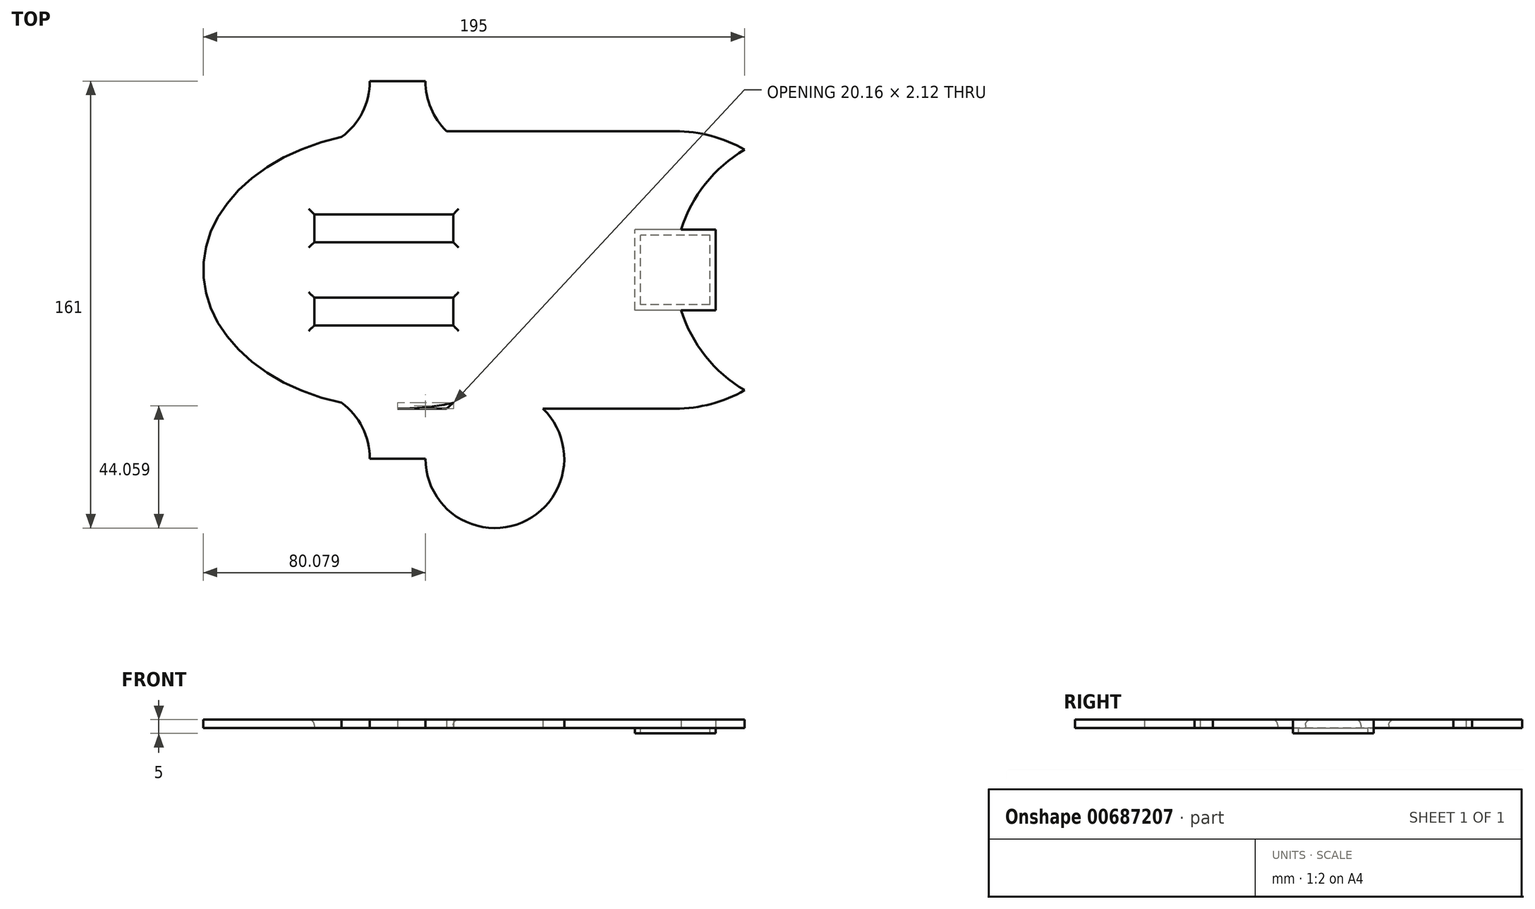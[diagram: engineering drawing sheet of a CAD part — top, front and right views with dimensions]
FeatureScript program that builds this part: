
annotation { "Feature Type Name" : "Feature", "Feature Type Description" : "" }
export const myFeature = defineFeature(function(context is Context, id is Id, definition is map)
    precondition{}
    {
        {
            var Q0;
            Q0=qCreatedBy(makeId("Top.planeOp"),FACE);
            var sketch = newSketch(context, id + "F0", { "sketchPlane" : qUnion([Q0])});
            skLineSegment(sketch, "E0.bottom", {"start": v(0, 0) * mm, "end": v(100, 0) * mm});
            skLineSegment(sketch, "E0.top", {"start": v(0, 100) * mm, "end": v(100, 100) * mm});
            skLineSegment(sketch, "E0.left", {"start": v(0, 0) * mm, "end": v(0, 30) * mm});
            skLineSegment(sketch, "E1", {"start": v(0, 50) * mm, "end": v(-70, 50) * mm});
            skEllipse(sketch, "E2", {"center": v(0, 50) * mm, "majorRadius": 50 * mm, "minorRadius": 70 * mm, "majorAxis": v(0, 1)});
            skLineSegment(sketch, "E3", {"start": v(0, 100) * mm, "end": v(0, 118) * mm});
            skLineSegment(sketch, "E4", {"start": v(0, 118) * mm, "end": v(10, 118) * mm});
            skLineSegment(sketch, "E5", {"start": v(0, 118) * mm, "end": v(-10, 118) * mm});
            skLineSegment(sketch, "E6", {"start": v(-10, 118) * mm, "end": v(-35, 118) * mm});
            skLineSegment(sketch, "E7", {"start": v(10, 118) * mm, "end": v(35, 118) * mm});
            skArc(sketch, "E8", {"start": v(-20.16, 97.88) * mm, "mid": v(-12.68, 106.73) * mm, "end": v(-10, 118) * mm});
            skCircle(sketch, "E9", {"center": v(35, 118) * mm, "radius": 25 * mm});
            skArc(sketch, "E10.MirrorC", {"start": v(-35.7, 93) * mm, "mid": v(-42.48, 141.85) * mm, "end": v(-20.16, 97.88) * mm});
            skCircle(sketch, "E11.MirrorC", {"center": v(-35, -18) * mm, "radius": 25 * mm});
            skLineSegment(sketch, "E12.MirrorCS", {"start": v(-10, -18) * mm, "end": v(-35, -18) * mm});
            skLineSegment(sketch, "E13.MirrorCS", {"start": v(0, -18) * mm, "end": v(10, -18) * mm});
            skLineSegment(sketch, "E14.MirrorCS", {"start": v(0, -18) * mm, "end": v(-10, -18) * mm});
            skLineSegment(sketch, "E15.MirrorCS", {"start": v(0, 0) * mm, "end": v(0, -18) * mm});
            skCircle(sketch, "E16.MirrorC", {"center": v(35, -18) * mm, "radius": 25 * mm});
            skLineSegment(sketch, "E17.MirrorCS", {"start": v(10, -18) * mm, "end": v(35, -18) * mm});
            skArc(sketch, "E18", {"start": v(-10, 118) * mm, "mid": v(-12.68, 106.73) * mm, "end": v(-20.16, 97.88) * mm});
            skLineSegment(sketch, "E19", {"start": v(150, 50) * mm, "end": v(0, 50) * mm});
            skArc(sketch, "E20", {"start": v(125, 93.3) * mm, "mid": v(100, 50) * mm, "end": v(125, 6.7) * mm});
            skCircle(sketch, "E21", {"center": v(100, 50) * mm, "radius": 50 * mm});
            skLineSegment(sketch, "E22", {"start": v(0, 50) * mm, "end": v(0, 60) * mm});
            skLineSegment(sketch, "E23", {"start": v(0, 60) * mm, "end": v(-10, 60) * mm});
            skLineSegment(sketch, "E24", {"start": v(-10, 40) * mm, "end": v(0, 40) * mm});
            skLineSegment(sketch, "E25.top", {"start": v(0, 70) * mm, "end": v(-10, 70) * mm});
            skLineSegment(sketch, "E26.top", {"start": v(-10, 30) * mm, "end": v(0, 30) * mm});
            skLineSegment(sketch, "E27", {"start": v(-10, 70) * mm, "end": v(-30, 70) * mm});
            skLineSegment(sketch, "E28", {"start": v(-30, 70) * mm, "end": v(-30, 60) * mm});
            skLineSegment(sketch, "E29", {"start": v(-30, 60) * mm, "end": v(-10, 60) * mm});
            skLineSegment(sketch, "E30", {"start": v(0, 70) * mm, "end": v(20, 70) * mm});
            skLineSegment(sketch, "E31", {"start": v(20, 70) * mm, "end": v(20, 60) * mm});
            skLineSegment(sketch, "E32", {"start": v(20, 60) * mm, "end": v(0, 60) * mm});
            skLineSegment(sketch, "E33", {"start": v(-10, 40) * mm, "end": v(-30, 40) * mm});
            skLineSegment(sketch, "E34", {"start": v(-30, 40) * mm, "end": v(-30, 30) * mm});
            skLineSegment(sketch, "E35", {"start": v(-30, 30) * mm, "end": v(20, 30) * mm});
            skLineSegment(sketch, "E36", {"start": v(20, 30) * mm, "end": v(20, 40) * mm});
            skLineSegment(sketch, "E37", {"start": v(20, 40) * mm, "end": v(0, 40) * mm});
            skLineSegment(sketch, "E38", {"start": v(0, 40) * mm, "end": v(0, 60) * mm});
            skLineSegment(sketch, "E39", {"start": v(0, 70) * mm, "end": v(0, 100) * mm});
            skPoint(sketch, "E40.orphan", {"position": v(150, 100) * mm});
            skLineSegment(sketch, "E41.bottom", {"start": v(112.5, 37.5) * mm, "end": v(87.5, 37.5) * mm});
            skLineSegment(sketch, "E41.top", {"start": v(112.5, 62.5) * mm, "end": v(87.5, 62.5) * mm});
            skLineSegment(sketch, "E41.left", {"start": v(112.5, 37.5) * mm, "end": v(112.5, 62.5) * mm});
            skLineSegment(sketch, "E41.right", {"start": v(87.5, 37.5) * mm, "end": v(87.5, 62.5) * mm});
            skLineSegment(sketch, "E42.0", {"start": v(114.5, 64.5) * mm, "end": v(85.5, 64.5) * mm});
            skLineSegment(sketch, "E42.1", {"start": v(114.5, 35.5) * mm, "end": v(114.5, 64.5) * mm});
            skLineSegment(sketch, "E42.2", {"start": v(114.5, 35.5) * mm, "end": v(85.5, 35.5) * mm});
            skLineSegment(sketch, "E42.3", {"start": v(85.5, 35.5) * mm, "end": v(85.5, 64.5) * mm});
            skSolve(sketch);
        }
        {
            var Q0;
            {var subQ0=sQuery(id+"F0.wireOp",EDGE,"E11.MirrorC");var subQ1=sQuery(id+"F0.wireOp",EDGE,"E2");var subQ2=makeQuery(id+"F0.imprint","INTERSECT",VERTEX,{"disambiguationData":[OD(0.0)],"derivedFrom":[subQ1,subQ0]});Q0=makeQuery(id+"F0.imprint","IMPRINT",FACE,{"disambiguationData":[TD([[makeQuery(id+"F0.imprint","IMPRINT",EDGE,{"disambiguationData":[TD([[subQ2,-1.0]])],"derivedFrom":subQ1}),1.0]])]});}
            var Q1;
            {var subQ4=sQuery(id+"F0.wireOp",EDGE,"E13.MirrorCS");Q1=makeQuery(id+"F0.imprint","IMPRINT",FACE,{"disambiguationData":[TD([[makeQuery(id+"F0.imprint","IMPRINT",EDGE,{"derivedFrom":subQ4}),1.0]])]});}
            var Q2;
            {var subQ0=sQuery(id+"F0.wireOp",EDGE,"E21");var subQ1=sQuery(id+"F0.wireOp",EDGE,"E0.bottom");var subQ2=makeQuery(id+"F0.imprint","INTERSECT",VERTEX,{"derivedFrom":[subQ1,subQ0]});Q2=makeQuery(id+"F0.imprint","IMPRINT",FACE,{"disambiguationData":[TD([[makeQuery(id+"F0.imprint","IMPRINT",EDGE,{"disambiguationData":[TD([[subQ2,1.0]])],"derivedFrom":subQ1}),1.0]])]});}
            var Q3;
            {var subQ0=sQuery(id+"F0.wireOp",EDGE,"E3");Q3=makeQuery(id+"F0.imprint","IMPRINT",FACE,{"disambiguationData":[TD([[makeQuery(id+"F0.imprint","IMPRINT",EDGE,{"derivedFrom":subQ0}),-1.0]])]});}
            var Q4;
            {var subQ0=sQuery(id+"F0.wireOp",EDGE,"E21");var subQ1=sQuery(id+"F0.wireOp",EDGE,"E0.top");var subQ2=makeQuery(id+"F0.imprint","INTERSECT",VERTEX,{"derivedFrom":[subQ1,subQ0]});Q4=makeQuery(id+"F0.imprint","IMPRINT",FACE,{"disambiguationData":[TD([[makeQuery(id+"F0.imprint","IMPRINT",EDGE,{"disambiguationData":[TD([[subQ2,1.0]])],"derivedFrom":subQ1}),-1.0]])]});}
            var Q5;
            {var subQ4=sQuery(id+"F0.wireOp",EDGE,"E14.MirrorCS");Q5=makeQuery(id+"F0.imprint","IMPRINT",FACE,{"disambiguationData":[TD([[makeQuery(id+"F0.imprint","IMPRINT",EDGE,{"derivedFrom":subQ4}),-1.0]])]});}
            var Q6;
            {var subQ0=sQuery(id+"F0.wireOp",EDGE,"E3");Q6=makeQuery(id+"F0.imprint","IMPRINT",FACE,{"disambiguationData":[TD([[makeQuery(id+"F0.imprint","IMPRINT",EDGE,{"derivedFrom":subQ0}),1.0]])]});}
            var Q7;
            {var subQ5=sQuery(id+"F0.wireOp",EDGE,"E21");var subQ6=sQuery(id+"F0.wireOp",EDGE,"E19");var subQ7=makeQuery(id+"F0.imprint","INTERSECT",VERTEX,{"disambiguationData":[OD(0.0)],"derivedFrom":[subQ6,subQ5]});Q7=makeQuery(id+"F0.imprint","IMPRINT",FACE,{"disambiguationData":[TD([[makeQuery(id+"F0.imprint","IMPRINT",EDGE,{"disambiguationData":[TD([[subQ7,-1.0]])],"derivedFrom":subQ6}),-1.0]])]});}
            var Q8;
            {var subQ3=sQuery(id+"F0.wireOp",EDGE,"E19");var subQ5=sQuery(id+"F0.wireOp",EDGE,"E21");var subQ6=makeQuery(id+"F0.imprint","INTERSECT",VERTEX,{"disambiguationData":[OD(0.0)],"derivedFrom":[subQ3,subQ5]});Q8=makeQuery(id+"F0.imprint","IMPRINT",FACE,{"disambiguationData":[TD([[makeQuery(id+"F0.imprint","IMPRINT",EDGE,{"disambiguationData":[TD([[subQ6,-1.0]])],"derivedFrom":subQ3}),1.0]])]});}
            var Q9;
            {var subQ0=sQuery(id+"F0.wireOp",EDGE,"E16.MirrorC");var subQ1=sQuery(id+"F0.wireOp",EDGE,"E0.bottom");var subQ2=makeQuery(id+"F0.imprint","INTERSECT",VERTEX,{"disambiguationData":[OD(0.0)],"derivedFrom":[subQ1,subQ0]});Q9=makeQuery(id+"F0.imprint","IMPRINT",FACE,{"disambiguationData":[TD([[makeQuery(id+"F0.imprint","IMPRINT",EDGE,{"disambiguationData":[TD([[subQ2,1.0]])],"derivedFrom":subQ1}),1.0]])]});}
            var Q10;
            {var subQ0=sQuery(id+"F0.wireOp",EDGE,"E9");var subQ1=sQuery(id+"F0.wireOp",EDGE,"E0.top");var subQ2=makeQuery(id+"F0.imprint","INTERSECT",VERTEX,{"disambiguationData":[OD(0.0)],"derivedFrom":[subQ1,subQ0]});Q10=makeQuery(id+"F0.imprint","IMPRINT",FACE,{"disambiguationData":[TD([[makeQuery(id+"F0.imprint","IMPRINT",EDGE,{"disambiguationData":[TD([[subQ2,1.0]])],"derivedFrom":subQ1}),-1.0]])]});}
            var Q11;
            {var subQ1=sQuery(id+"F0.wireOp",EDGE,"E0.left");Q11=makeQuery(id+"F0.imprint","IMPRINT",FACE,{"disambiguationData":[TD([[makeQuery(id+"F0.imprint","IMPRINT",EDGE,{"derivedFrom":subQ1}),1.0]])]});}
            var Q12;
            {var subQ1=sQuery(id+"F0.wireOp",EDGE,"E1");Q12=makeQuery(id+"F0.imprint","IMPRINT",FACE,{"disambiguationData":[TD([[makeQuery(id+"F0.imprint","IMPRINT",EDGE,{"derivedFrom":subQ1}),-1.0]])]});}
            var Q13;
            {var subQ0=sQuery(id+"F0.wireOp",EDGE,"E21");var subQ2=sQuery(id+"F0.wireOp",EDGE,"E2");var subQ3=makeQuery(id+"F0.imprint","INTERSECT",VERTEX,{"disambiguationData":[OD(0.0)],"derivedFrom":[subQ2,subQ0]});Q13=makeQuery(id+"F0.imprint","IMPRINT",FACE,{"disambiguationData":[TD([[makeQuery(id+"F0.imprint","IMPRINT",EDGE,{"disambiguationData":[TD([[subQ3,-1.0]])],"derivedFrom":subQ2}),-1.0]])]});}
            var Q14;
            {var subQ6=sQuery(id+"F0.wireOp",EDGE,"E19");var subQ7=sQuery(id+"F0.wireOp",EDGE,"E2");var subQ8=makeQuery(id+"F0.imprint","INTERSECT",VERTEX,{"derivedFrom":[subQ7,subQ6]});Q14=makeQuery(id+"F0.imprint","IMPRINT",FACE,{"disambiguationData":[TD([[makeQuery(id+"F0.imprint","IMPRINT",EDGE,{"disambiguationData":[TD([[subQ8,-1.0]])],"derivedFrom":subQ7}),-1.0]])]});}
            var Q15;
            Q15=makeQuery(id+"F0.imprint","IMPRINT",FACE,{"disambiguationData":[TD([[makeQuery(id+"F0.imprint","IMPRINT",EDGE,{"derivedFrom":sQuery(id+"F0.wireOp",EDGE,"E30")}),1.0]])]});
            var Q16;
            {var subQ0=sQuery(id+"F0.wireOp",EDGE,"E19");var subQ1=sQuery(id+"F0.wireOp",EDGE,"E2");var subQ2=makeQuery(id+"F0.imprint","INTERSECT",VERTEX,{"derivedFrom":[subQ1,subQ0]});Q16=makeQuery(id+"F0.imprint","IMPRINT",FACE,{"disambiguationData":[TD([[makeQuery(id+"F0.imprint","IMPRINT",EDGE,{"disambiguationData":[TD([[subQ2,-1.0]])],"derivedFrom":subQ1}),1.0]])]});}
            var Q17;
            {var subQ0=sQuery(id+"F0.wireOp",EDGE,"E21");var subQ1=sQuery(id+"F0.wireOp",EDGE,"E2");var subQ2=makeQuery(id+"F0.imprint","INTERSECT",VERTEX,{"disambiguationData":[OD(0.0)],"derivedFrom":[subQ1,subQ0]});Q17=makeQuery(id+"F0.imprint","IMPRINT",FACE,{"disambiguationData":[TD([[makeQuery(id+"F0.imprint","IMPRINT",EDGE,{"disambiguationData":[TD([[subQ2,-1.0]])],"derivedFrom":subQ1}),1.0]])]});}
            var Q18;
            {var subQ4=sQuery(id+"F0.wireOp",EDGE,"E0.left");Q18=makeQuery(id+"F0.imprint","IMPRINT",FACE,{"disambiguationData":[TD([[makeQuery(id+"F0.imprint","IMPRINT",EDGE,{"derivedFrom":subQ4}),-1.0]])]});}
            var Q19;
            {var subQ1=sQuery(id+"F0.wireOp",EDGE,"E0.top");var subQ3=sQuery(id+"F0.wireOp",EDGE,"E9");var subQ4=makeQuery(id+"F0.imprint","INTERSECT",VERTEX,{"disambiguationData":[OD(1.0)],"derivedFrom":[subQ1,subQ3]});Q19=makeQuery(id+"F0.imprint","IMPRINT",FACE,{"disambiguationData":[TD([[makeQuery(id+"F0.imprint","IMPRINT",EDGE,{"disambiguationData":[TD([[subQ4,-1.0]])],"derivedFrom":subQ3}),-1.0]])]});}
            var Q20;
            {var subQ0=sQuery(id+"F0.wireOp",EDGE,"E9");var subQ1=sQuery(id+"F0.wireOp",EDGE,"E2");var subQ2=makeQuery(id+"F0.imprint","INTERSECT",VERTEX,{"disambiguationData":[OD(0.0)],"derivedFrom":[subQ1,subQ0]});Q20=makeQuery(id+"F0.imprint","IMPRINT",FACE,{"disambiguationData":[TD([[makeQuery(id+"F0.imprint","IMPRINT",EDGE,{"disambiguationData":[TD([[subQ2,-1.0]])],"derivedFrom":subQ1}),1.0]])]});}
            var Q21;
            {var subQ1=sQuery(id+"F0.wireOp",EDGE,"E0.bottom");var subQ3=sQuery(id+"F0.wireOp",EDGE,"E16.MirrorC");var subQ4=makeQuery(id+"F0.imprint","INTERSECT",VERTEX,{"disambiguationData":[OD(1.0)],"derivedFrom":[subQ1,subQ3]});Q21=makeQuery(id+"F0.imprint","IMPRINT",FACE,{"disambiguationData":[TD([[makeQuery(id+"F0.imprint","IMPRINT",EDGE,{"disambiguationData":[TD([[subQ4,-1.0]])],"derivedFrom":subQ3}),1.0]])]});}
            var Q22;
            {var subQ0=sQuery(id+"F0.wireOp",EDGE,"E16.MirrorC");var subQ1=sQuery(id+"F0.wireOp",EDGE,"E2");var subQ2=makeQuery(id+"F0.imprint","INTERSECT",VERTEX,{"disambiguationData":[OD(0.0)],"derivedFrom":[subQ1,subQ0]});Q22=makeQuery(id+"F0.imprint","IMPRINT",FACE,{"disambiguationData":[TD([[makeQuery(id+"F0.imprint","IMPRINT",EDGE,{"disambiguationData":[TD([[subQ2,-1.0]])],"derivedFrom":subQ1}),1.0]])]});}
            var Q23;
            {var subQ3=sQuery(id+"F0.wireOp",EDGE,"E19");var subQ9=sQuery(id+"F0.wireOp",EDGE,"E42.1");var subQ10=makeQuery(id+"F0.imprint","INTERSECT",VERTEX,{"derivedFrom":[subQ3,subQ9]});Q23=makeQuery(id+"F0.imprint","IMPRINT",FACE,{"disambiguationData":[TD([[makeQuery(id+"F0.imprint","IMPRINT",EDGE,{"disambiguationData":[TD([[subQ10,-1.0]])],"derivedFrom":subQ3}),1.0]])]});}
            var Q24;
            {var subQ0=sQuery(id+"F0.wireOp",EDGE,"E41.right");var subQ3=sQuery(id+"F0.wireOp",EDGE,"E19");var subQ4=makeQuery(id+"F0.imprint","INTERSECT",VERTEX,{"derivedFrom":[subQ3,subQ0]});Q24=makeQuery(id+"F0.imprint","IMPRINT",FACE,{"disambiguationData":[TD([[makeQuery(id+"F0.imprint","IMPRINT",EDGE,{"disambiguationData":[TD([[subQ4,-1.0]])],"derivedFrom":subQ3}),1.0]])]});}
            var Q25;
            {var subQ0=sQuery(id+"F0.wireOp",EDGE,"E20");var subQ1=sQuery(id+"F0.wireOp",EDGE,"E19");var subQ2=makeQuery(id+"F0.imprint","INTERSECT",VERTEX,{"derivedFrom":[subQ1,subQ0]});Q25=makeQuery(id+"F0.imprint","IMPRINT",FACE,{"disambiguationData":[TD([[makeQuery(id+"F0.imprint","IMPRINT",EDGE,{"disambiguationData":[TD([[subQ2,-1.0]])],"derivedFrom":subQ1}),1.0]])]});}
            var Q26;
            {var subQ0=sQuery(id+"F0.wireOp",EDGE,"E20");var subQ1=sQuery(id+"F0.wireOp",EDGE,"E19");var subQ2=makeQuery(id+"F0.imprint","INTERSECT",VERTEX,{"derivedFrom":[subQ1,subQ0]});Q26=makeQuery(id+"F0.imprint","IMPRINT",FACE,{"disambiguationData":[TD([[makeQuery(id+"F0.imprint","IMPRINT",EDGE,{"disambiguationData":[TD([[subQ2,-1.0]])],"derivedFrom":subQ1}),-1.0]])]});}
            var Q27;
            {var subQ7=sQuery(id+"F0.wireOp",EDGE,"E19");var subQ9=sQuery(id+"F0.wireOp",EDGE,"E42.1");var subQ10=makeQuery(id+"F0.imprint","INTERSECT",VERTEX,{"derivedFrom":[subQ7,subQ9]});Q27=makeQuery(id+"F0.imprint","IMPRINT",FACE,{"disambiguationData":[TD([[makeQuery(id+"F0.imprint","IMPRINT",EDGE,{"disambiguationData":[TD([[subQ10,-1.0]])],"derivedFrom":subQ7}),-1.0]])]});}
            var Q28;
            {var subQ0=sQuery(id+"F0.wireOp",EDGE,"E41.left");var subQ1=sQuery(id+"F0.wireOp",EDGE,"E19");var subQ2=makeQuery(id+"F0.imprint","INTERSECT",VERTEX,{"derivedFrom":[subQ1,subQ0]});Q28=makeQuery(id+"F0.imprint","IMPRINT",FACE,{"disambiguationData":[TD([[makeQuery(id+"F0.imprint","IMPRINT",EDGE,{"disambiguationData":[TD([[subQ2,-1.0]])],"derivedFrom":subQ1}),1.0]])]});}
            var Q29;
            {var subQ0=sQuery(id+"F0.wireOp",EDGE,"E41.left");var subQ1=sQuery(id+"F0.wireOp",EDGE,"E19");var subQ2=makeQuery(id+"F0.imprint","INTERSECT",VERTEX,{"derivedFrom":[subQ1,subQ0]});Q29=makeQuery(id+"F0.imprint","IMPRINT",FACE,{"disambiguationData":[TD([[makeQuery(id+"F0.imprint","IMPRINT",EDGE,{"disambiguationData":[TD([[subQ2,-1.0]])],"derivedFrom":subQ1}),-1.0]])]});}
            var Q30;
            {var subQ0=sQuery(id+"F0.wireOp",EDGE,"E41.right");var subQ3=sQuery(id+"F0.wireOp",EDGE,"E19");var subQ4=makeQuery(id+"F0.imprint","INTERSECT",VERTEX,{"derivedFrom":[subQ3,subQ0]});Q30=makeQuery(id+"F0.imprint","IMPRINT",FACE,{"disambiguationData":[TD([[makeQuery(id+"F0.imprint","IMPRINT",EDGE,{"disambiguationData":[TD([[subQ4,-1.0]])],"derivedFrom":subQ3}),-1.0]])]});}
            extrude(context, id + "F1", {"entities" : qUnion([Q0, Q1, Q2, Q3, Q4, Q5, Q6, Q7, Q8, Q9, Q10, Q11, Q12, Q13, Q14, Q15, Q16, Q17, Q18, Q19, Q20, Q21, Q22, Q23, Q24, Q25, Q26, Q27, Q28, Q29, Q30]), "depth" : 3 * mm, "offsetDistance" : 25 * mm});
        }
        {
            var Q0;
            Q0=makeQuery(id+"F1.opExtrude","CAP_EDGE",EDGE,{"disambiguationData":[OSD([sQuery(id+"F0.wireOp",EDGE,"E31")])],"isStart":false});
            var Q1;
            Q1=makeQuery(id+"F1.opExtrude","CAP_EDGE",EDGE,{"disambiguationData":[OSD([sQuery(id+"F0.wireOp",EDGE,"E36")])],"isStart":false});
            var Q2;
            Q2=makeQuery(id+"F1.opExtrude","CAP_EDGE",EDGE,{"disambiguationData":[OSD([sQuery(id+"F0.wireOp",EDGE,"E24"),sQuery(id+"F0.wireOp",EDGE,"E33"),sQuery(id+"F0.wireOp",EDGE,"E37")])],"isStart":false});
            var Q3;
            Q3=makeQuery(id+"F1.opExtrude","CAP_EDGE",EDGE,{"disambiguationData":[OSD([sQuery(id+"F0.wireOp",EDGE,"E23"),sQuery(id+"F0.wireOp",EDGE,"E29"),sQuery(id+"F0.wireOp",EDGE,"E32")])],"isStart":false});
            var Q4;
            Q4=makeQuery(id+"F1.opExtrude","CAP_EDGE",EDGE,{"disambiguationData":[OSD([sQuery(id+"F0.wireOp",EDGE,"E35")])],"isStart":false});
            var Q5;
            Q5=makeQuery(id+"F1.opExtrude","CAP_EDGE",EDGE,{"disambiguationData":[OSD([sQuery(id+"F0.wireOp",EDGE,"E34")])],"isStart":false});
            var Q6;
            Q6=makeQuery(id+"F1.opExtrude","CAP_EDGE",EDGE,{"disambiguationData":[OSD([sQuery(id+"F0.wireOp",EDGE,"E28")])],"isStart":false});
            var Q7;
            Q7=makeQuery(id+"F1.opExtrude","CAP_EDGE",EDGE,{"disambiguationData":[OSD([sQuery(id+"F0.wireOp",EDGE,"E25.top"),sQuery(id+"F0.wireOp",EDGE,"E27"),sQuery(id+"F0.wireOp",EDGE,"E30")])],"isStart":false});
            var Q8;
            Q8=makeQuery(id+"FWjQsiPRKmnbxU6_1.boolean.opBoolean","COPY",EDGE,{"derivedFrom":makeQuery(id+"FWjQsiPRKmnbxU6_1.opExtrude","CAP_EDGE",EDGE,{"disambiguationData":[OSD([sQuery(id+"FoRDWVH2EN1YLIM_1.wireOp",EDGE,"Fo7FTBvF-OatF-Ye8v-invw-BYf8DDfDNs5p")])],"isStart":true})});
            var Q9;
            Q9=makeQuery(id+"FWjQsiPRKmnbxU6_1.boolean.opBoolean","INTERSECT",EDGE,{"derivedFrom":[makeQuery(id+"FhsavfPUiMTL5cG_1.opExtrude","SWEPT_FACE",FACE,{"disambiguationData":[OSD([sQuery(id+"FaphtbvGcqO1CS2_1.wireOp",EDGE,"SVR6mZwb-6mZz-pFOT-4R3M-2uJUIevgwBhd.right"),sQuery(id+"FaphtbvGcqO1CS2_1.wireOp",EDGE,"BLSzf8hX-9h4d-mfL5-Iacp-5Haw44lP9nYf.left")])]}),makeQuery(id+"FWjQsiPRKmnbxU6_1.opExtrude","SWEPT_FACE",FACE,{"disambiguationData":[OSD([sQuery(id+"FoRDWVH2EN1YLIM_1.wireOp",EDGE,"Fo7FTBvF-OatF-Ye8v-invw-BYf8DDfDNs5p")])]})]});
            var Q10;
            Q10=makeQuery(id+"FWjQsiPRKmnbxU6_1.boolean.opBoolean","COPY",EDGE,{"derivedFrom":makeQuery(id+"FWjQsiPRKmnbxU6_1.opExtrude","CAP_EDGE",EDGE,{"disambiguationData":[OSD([sQuery(id+"FoRDWVH2EN1YLIM_1.wireOp",EDGE,"f88abefe-f133-40e1-8b6e-ae7882c6de267.MirrorC")])],"isStart":true})});
            var Q11;
            Q11=makeQuery(id+"FWjQsiPRKmnbxU6_1.boolean.opBoolean","INTERSECT",EDGE,{"derivedFrom":[makeQuery(id+"FhsavfPUiMTL5cG_1.opExtrude","SWEPT_FACE",FACE,{"disambiguationData":[OSD([sQuery(id+"FaphtbvGcqO1CS2_1.wireOp",EDGE,"aa437bf4-4790-4772-8fad-b6166ee4a9c60.MirrorCS"),sQuery(id+"FaphtbvGcqO1CS2_1.wireOp",EDGE,"c2af337a-7aa6-4700-ac16-6fe0a1636ed80.MirrorCS")])]}),makeQuery(id+"FWjQsiPRKmnbxU6_1.opExtrude","SWEPT_FACE",FACE,{"disambiguationData":[OSD([sQuery(id+"FoRDWVH2EN1YLIM_1.wireOp",EDGE,"f88abefe-f133-40e1-8b6e-ae7882c6de267.MirrorC")])]})]});
            fillet(context, id + "F2", {"entities" : qUnion([Q0, Q1, Q2, Q3, Q4, Q5, Q6, Q7, Q8, Q9, Q10, Q11]), "radius" : 2 * mm, "tangentPropagation" : true, "allowEdgeOverflow" : false});
        }
        {
            var Q0;
            {var subQ0=sQuery(id+"F0.wireOp",EDGE,"E41.right");var subQ3=sQuery(id+"F0.wireOp",EDGE,"E19");var subQ4=makeQuery(id+"F0.imprint","INTERSECT",VERTEX,{"derivedFrom":[subQ3,subQ0]});Q0=makeQuery(id+"F0.imprint","IMPRINT",FACE,{"disambiguationData":[TD([[makeQuery(id+"F0.imprint","IMPRINT",EDGE,{"disambiguationData":[TD([[subQ4,-1.0]])],"derivedFrom":subQ3}),1.0]])]});}
            var Q1;
            {var subQ3=sQuery(id+"F0.wireOp",EDGE,"E19");var subQ9=sQuery(id+"F0.wireOp",EDGE,"E42.1");var subQ10=makeQuery(id+"F0.imprint","INTERSECT",VERTEX,{"derivedFrom":[subQ3,subQ9]});Q1=makeQuery(id+"F0.imprint","IMPRINT",FACE,{"disambiguationData":[TD([[makeQuery(id+"F0.imprint","IMPRINT",EDGE,{"disambiguationData":[TD([[subQ10,-1.0]])],"derivedFrom":subQ3}),1.0]])]});}
            var Q2;
            {var subQ7=sQuery(id+"F0.wireOp",EDGE,"E19");var subQ9=sQuery(id+"F0.wireOp",EDGE,"E42.1");var subQ10=makeQuery(id+"F0.imprint","INTERSECT",VERTEX,{"derivedFrom":[subQ7,subQ9]});Q2=makeQuery(id+"F0.imprint","IMPRINT",FACE,{"disambiguationData":[TD([[makeQuery(id+"F0.imprint","IMPRINT",EDGE,{"disambiguationData":[TD([[subQ10,-1.0]])],"derivedFrom":subQ7}),-1.0]])]});}
            var Q3;
            {var subQ0=sQuery(id+"F0.wireOp",EDGE,"E41.right");var subQ3=sQuery(id+"F0.wireOp",EDGE,"E19");var subQ4=makeQuery(id+"F0.imprint","INTERSECT",VERTEX,{"derivedFrom":[subQ3,subQ0]});Q3=makeQuery(id+"F0.imprint","IMPRINT",FACE,{"disambiguationData":[TD([[makeQuery(id+"F0.imprint","IMPRINT",EDGE,{"disambiguationData":[TD([[subQ4,-1.0]])],"derivedFrom":subQ3}),-1.0]])]});}
            extrude(context, id + "F3", {"entities" : qUnion([Q0, Q1, Q2, Q3]), "operationType" : NewBodyOperationType.ADD, "oppositeDirection" : true, "depth" : 2 * mm, "offsetDistance" : 25 * mm});
        }
    });
